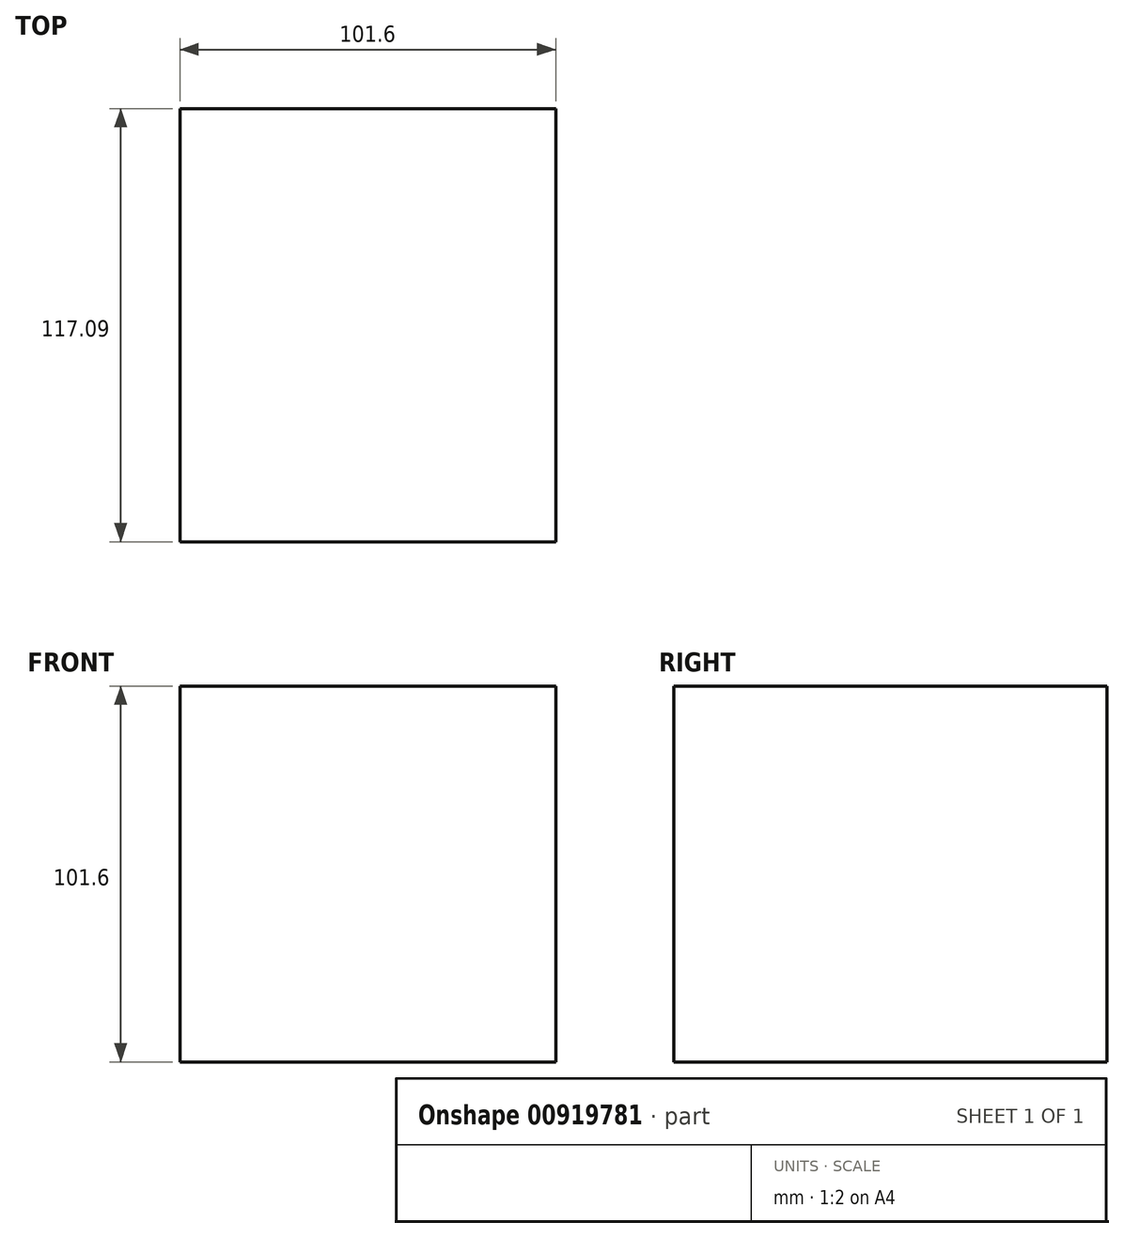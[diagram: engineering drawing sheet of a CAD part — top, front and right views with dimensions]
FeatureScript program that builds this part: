
annotation { "Feature Type Name" : "Feature", "Feature Type Description" : "" }
export const myFeature = defineFeature(function(context is Context, id is Id, definition is map)
    precondition{}
    {
        {
            var Q0;
            Q0=qCreatedBy(makeId("Front.planeOp"),FACE);
            var sketch = newSketch(context, id + "F0", { "sketchPlane" : qUnion([Q0])});
            skLineSegment(sketch, "E0.bottom", {"start": v(-50.8, 59.02) * mm, "end": v(50.8, 59.02) * mm});
            skLineSegment(sketch, "E0.top", {"start": v(-50.8, -42.58) * mm, "end": v(50.8, -42.58) * mm});
            skLineSegment(sketch, "E0.left", {"start": v(-50.8, 59.02) * mm, "end": v(-50.8, -42.58) * mm});
            skLineSegment(sketch, "E0.right", {"start": v(50.8, 59.02) * mm, "end": v(50.8, -42.58) * mm});
            skSolve(sketch);
        }
        {
            var Q0;
            Q0=makeQuery(id+"F0.imprint","IMPRINT",FACE,{"disambiguationData":[TD([[makeQuery(id+"F0.imprint","IMPRINT",EDGE,{"derivedFrom":sQuery(id+"F0.wireOp",EDGE,"E0.bottom")}),-1.0]])]});
            extrude(context, id + "F1", {"entities" : qUnion([Q0]), "depth" : 117.1 * mm, "offsetDistance" : 25.4 * mm});
        }
    });
